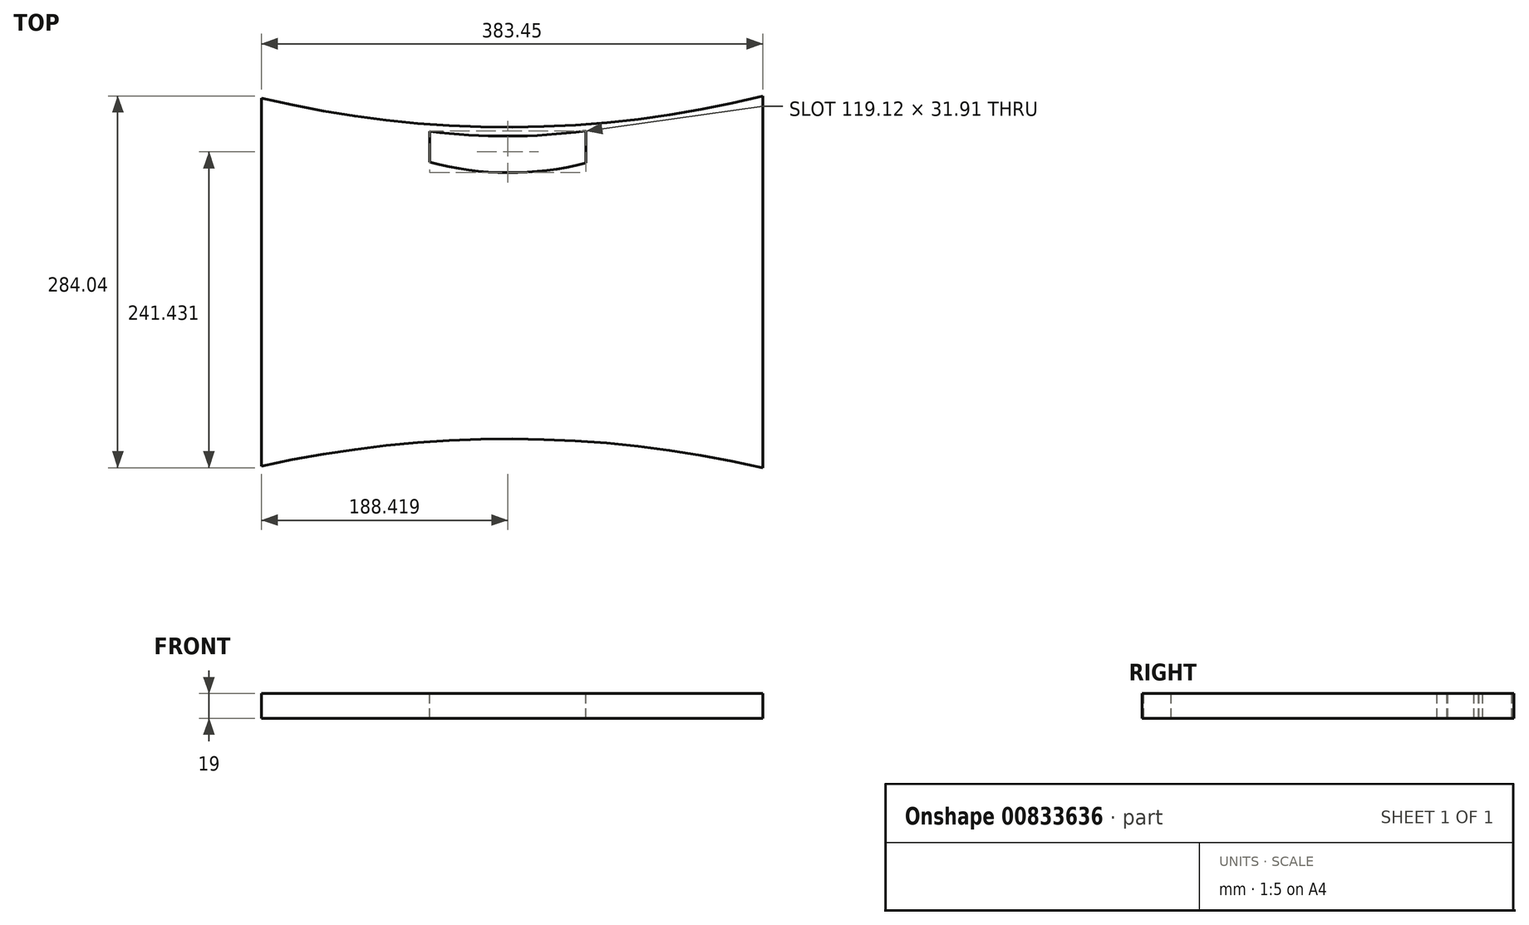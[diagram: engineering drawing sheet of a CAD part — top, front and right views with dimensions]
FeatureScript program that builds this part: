
annotation { "Feature Type Name" : "Feature", "Feature Type Description" : "" }
export const myFeature = defineFeature(function(context is Context, id is Id, definition is map)
    precondition{}
    {
        {
            var Q0;
            Q0=qCreatedBy(makeId("Top.planeOp"),FACE);
            var sketch = newSketch(context, id + "F0", { "sketchPlane" : qUnion([Q0])});
            skLineSegment(sketch, "E0.bottom", {"start": v(200, 170.33) * mm, "end": v(-200, 170.33) * mm});
            skLineSegment(sketch, "E0.top", {"start": v(200, -179.67) * mm, "end": v(-200, -179.67) * mm});
            skLineSegment(sketch, "E0.left", {"start": v(200, 170.33) * mm, "end": v(200, -179.67) * mm});
            skLineSegment(sketch, "E0.right", {"start": v(-200, 170.33) * mm, "end": v(-200, -179.67) * mm});
            skPoint(sketch, "E0.middle", {"position": v(0, -4.67) * mm});
            skSolve(sketch);
        }
        {
            var Q0;
            Q0=makeQuery(id+"F0.imprint","IMPRINT",FACE,{"disambiguationData":[TD([[makeQuery(id+"F0.imprint","IMPRINT",EDGE,{"derivedFrom":sQuery(id+"F0.wireOp",EDGE,"E0.bottom")}),1.0]])]});
            extrude(context, id + "F1", {"entities" : qUnion([Q0]), "depth" : 19 * mm, "offsetDistance" : 25 * mm});
        }
        {
            var Q0;
            Q0=makeQuery(id+"F1.opExtrude","CAP_FACE",FACE,{"disambiguationData":[OSD([sQuery(id+"F0.wireOp",EDGE,"E0.bottom"),sQuery(id+"F0.wireOp",EDGE,"E0.top"),sQuery(id+"F0.wireOp",EDGE,"E0.left"),sQuery(id+"F0.wireOp",EDGE,"E0.right")])],"isStart":false});
            var sketch = newSketch(context, id + "F2", { "sketchPlane" : qUnion([Q0])});
            skLineSegment(sketch, "E1", {"start": v(-191.45, -144.21) * mm, "end": v(-191.45, 137.22) * mm});
            skLineSegment(sketch, "E2", {"start": v(192, 138.7) * mm, "end": v(192, -145.33) * mm});
            skArc(sketch, "E3", {"start": v(-191.45, 137.22) * mm, "mid": v(0.37, 114.93) * mm, "end": v(192, 138.7) * mm});
            skArc(sketch, "E4", {"start": v(192, -145.33) * mm, "mid": v(0.34, -123.3) * mm, "end": v(-191.45, -144.21) * mm});
            skSolve(sketch);
        }
        {
            var Q0;
            Q0=makeQuery(id+"F2.imprint","IMPRINT",FACE,{"disambiguationData":[TD([[makeQuery(id+"F2.imprint","IMPRINT",EDGE,{"derivedFrom":sQuery(id+"F2.wireOp",EDGE,"E1")}),1.0]])]});
            extrude(context, id + "F3", {"entities" : qUnion([Q0]), "operationType" : NewBodyOperationType.REMOVE, "endBound" : BoundingType.THROUGH_ALL, "oppositeDirection" : true, "depth" : 25 * mm, "offsetDistance" : 25 * mm});
        }
        {
            var Q0;
            Q0=makeQuery(id+"F1.opExtrude","CAP_FACE",FACE,{"disambiguationData":[OSD([sQuery(id+"F0.wireOp",EDGE,"E0.bottom"),sQuery(id+"F0.wireOp",EDGE,"E0.top"),sQuery(id+"F0.wireOp",EDGE,"E0.left"),sQuery(id+"F0.wireOp",EDGE,"E0.right")])],"isStart":false});
            var sketch = newSketch(context, id + "F4", { "sketchPlane" : qUnion([Q0])});
            skLineSegment(sketch, "E5", {"start": v(-62.6, 111.7) * mm, "end": v(-62.6, 88.26) * mm});
            skLineSegment(sketch, "E6", {"start": v(56.53, 87.58) * mm, "end": v(56.53, 112.06) * mm});
            skArc(sketch, "E7", {"start": v(-62.6, 88.26) * mm, "mid": v(-3.08, 80.14) * mm, "end": v(56.53, 87.58) * mm});
            skArc(sketch, "E8", {"start": v(-62.6, 111.7) * mm, "mid": v(-3.02, 108.08) * mm, "end": v(56.53, 112.06) * mm});
            skSolve(sketch);
        }
        {
            var Q0;
            Q0=makeQuery(id+"F4.imprint","IMPRINT",FACE,{"disambiguationData":[TD([[makeQuery(id+"F4.imprint","IMPRINT",EDGE,{"derivedFrom":sQuery(id+"F4.wireOp",EDGE,"E5")}),1.0]])]});
            extrude(context, id + "F5", {"entities" : qUnion([Q0]), "operationType" : NewBodyOperationType.REMOVE, "endBound" : BoundingType.THROUGH_ALL, "oppositeDirection" : true, "depth" : 25 * mm, "offsetDistance" : 25 * mm});
        }
    });
